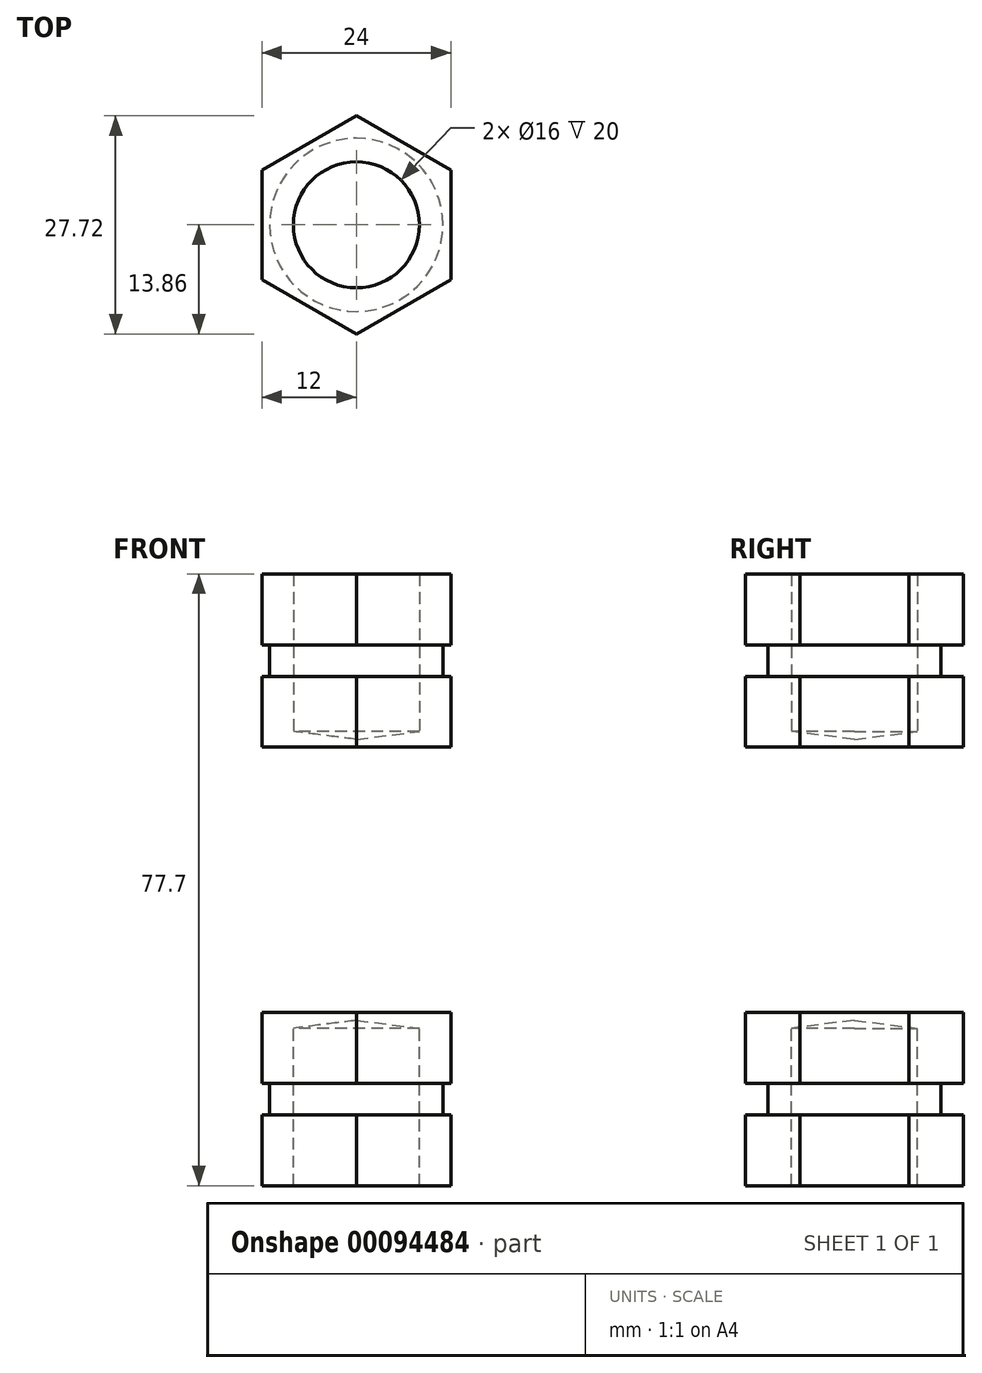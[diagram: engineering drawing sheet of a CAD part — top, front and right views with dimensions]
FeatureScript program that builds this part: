
annotation { "Feature Type Name" : "Feature", "Feature Type Description" : "" }
export const myFeature = defineFeature(function(context is Context, id is Id, definition is map)
    precondition{}
    {
        {
            var Q0;
            Q0=qCreatedBy(makeId("Top.planeOp"),FACE);
            var sketch = newSketch(context, id + "F0", { "sketchPlane" : qUnion([Q0])});
            skCircle(sketch, "E0", {"center": v(0, 0) * mm, "radius": 40.85 * mm});
            skSolve(sketch);
        }
        {
            var Q0;
            Q0=makeQuery(id+"F0.imprint","IMPRINT",FACE,{"disambiguationData":[TD([[makeQuery(id+"F0.imprint","IMPRINT",EDGE,{"derivedFrom":sQuery(id+"F0.wireOp",EDGE,"E0")}),1.0]])]});
            extrude(context, id + "F1", {"entities" : qUnion([Q0]), "depth" : 77.7 * mm});
        }
        {
            var Q0;
            Q0=makeQuery(id+"F1.opExtrude","CAP_FACE",FACE,{"disambiguationData":[OSD([sQuery(id+"F0.wireOp",EDGE,"E0")])],"isStart":true});
            var sketch = newSketch(context, id + "F2", { "sketchPlane" : qUnion([Q0])});
            skCircle(sketch, "E1.cCircle", {"center": v(0, 0) * mm, "radius": 12 * mm, "construction": true});
            skLineSegment(sketch, "E1.0", {"start": v(12, 6.93) * mm, "end": v(12, -6.93) * mm});
            skLineSegment(sketch, "E1.1", {"start": v(12, -6.93) * mm, "end": v(0, -13.86) * mm});
            skLineSegment(sketch, "E1.2", {"start": v(0, -13.86) * mm, "end": v(-12, -6.93) * mm});
            skLineSegment(sketch, "E1.3", {"start": v(-12, -6.93) * mm, "end": v(-12, 6.93) * mm});
            skLineSegment(sketch, "E1.4", {"start": v(-12, 6.93) * mm, "end": v(0, 13.86) * mm});
            skLineSegment(sketch, "E1.5", {"start": v(0, 13.86) * mm, "end": v(12, 6.93) * mm});
            skPoint(sketch, "E1.0.midPoint", {"position": v(12, 0) * mm});
            skCircle(sketch, "E2", {"center": v(0, 0) * mm, "radius": 8 * mm});
            skSolve(sketch);
        }
        {
            var Q0;
            Q0=makeQuery(id+"F2.imprint","IMPRINT",FACE,{"disambiguationData":[TD([[makeQuery(id+"F2.imprint","IMPRINT",EDGE,{"derivedFrom":sQuery(id+"F2.wireOp",EDGE,"E1.0")}),-1.0]])]});
            var Q1;
            Q1=makeQuery(id+"F2.imprint","IMPRINT",FACE,{"disambiguationData":[TD([[makeQuery(id+"F2.imprint","IMPRINT",EDGE,{"derivedFrom":sQuery(id+"F2.wireOp",EDGE,"E2")}),1.0]])]});
            extrude(context, id + "F3", {"entities" : qUnion([Q0, Q1]), "oppositeDirection" : true, "depth" : 22 * mm});
        }
        {
            var Q0;
            Q0=makeQuery(id+"F3.opExtrude","CAP_FACE",FACE,{"disambiguationData":[OSD([sQuery(id+"F2.wireOp",EDGE,"E1.0"),sQuery(id+"F2.wireOp",EDGE,"E1.1"),sQuery(id+"F2.wireOp",EDGE,"E1.2"),sQuery(id+"F2.wireOp",EDGE,"E1.3"),sQuery(id+"F2.wireOp",EDGE,"E1.4"),sQuery(id+"F2.wireOp",EDGE,"E1.5")])],"isStart":true});
            var sketch = newSketch(context, id + "F4", { "sketchPlane" : qUnion([Q0])});
            skCircle(sketch, "E3", {"center": v(0, 0) * mm, "radius": 15 * mm});
            skCircle(sketch, "E4", {"center": v(0, 0) * mm, "radius": 11 * mm});
            skSolve(sketch);
        }
        {
            var Q0;
            Q0=makeQuery(id+"F4.imprint","IMPRINT",FACE,{"disambiguationData":[TD([[makeQuery(id+"F4.imprint","IMPRINT",EDGE,{"derivedFrom":sQuery(id+"F4.wireOp",EDGE,"E3")}),1.0]])]});
            var Q1;
            Q1=makeQuery(id+"F4.imprint","IMPRINT",FACE,{"disambiguationData":[TD([[makeQuery(id+"F4.imprint","IMPRINT",EDGE,{"derivedFrom":sQuery(id+"F4.wireOp",EDGE,"E4")}),-1.0]])]});
            extrude(context, id + "F5", {"entities" : qUnion([Q0, Q1]), "operationType" : NewBodyOperationType.REMOVE, "oppositeDirection" : true, "depth" : 13 * mm, "hasSecondDirection" : true, "secondDirectionOppositeDirection" : true, "secondDirectionDepth" : 9 * mm});
        }
        {
            var Q0;
            Q0=makeQuery(id+"F3.opExtrude","SWEPT_BODY",BODY,{"disambiguationData":[OSD([sQuery(id+"F2.wireOp",EDGE,"E1.0"),sQuery(id+"F2.wireOp",EDGE,"E1.1"),sQuery(id+"F2.wireOp",EDGE,"E1.2"),sQuery(id+"F2.wireOp",EDGE,"E1.3"),sQuery(id+"F2.wireOp",EDGE,"E1.4"),sQuery(id+"F2.wireOp",EDGE,"E1.5")])]});
            var Q1;
            Q1=makeQuery(id+"F1.opExtrude","SWEPT_BODY",BODY,{"disambiguationData":[OSD([sQuery(id+"F0.wireOp",EDGE,"E0")])]});
            booleanBodies(context, id + "F6", {"operationType" : BooleanOperationType.SUBTRACTION, "tools" : qUnion([Q0]), "targets" : qUnion([Q1]), "keepTools" : true});
        }
        {
            var Q0;
            Q0=qCreatedBy(makeId("Front.planeOp"),FACE);
            var sketch = newSketch(context, id + "F7", { "sketchPlane" : qUnion([Q0])});
            skLineSegment(sketch, "E5", {"start": v(0, 0) * mm, "end": v(0, 21) * mm});
            skLineSegment(sketch, "E6", {"start": v(0, 21) * mm, "end": v(8, 20) * mm});
            skLineSegment(sketch, "E7", {"start": v(8, 20) * mm, "end": v(8, 0) * mm});
            skLineSegment(sketch, "E8", {"start": v(8, 0) * mm, "end": v(0, 0) * mm});
            skSolve(sketch);
        }
        {
            var Q0;
            Q0=makeQuery(id+"F7.imprint","IMPRINT",FACE,{"disambiguationData":[TD([[makeQuery(id+"F7.imprint","IMPRINT",EDGE,{"derivedFrom":sQuery(id+"F7.wireOp",EDGE,"E5")}),-1.0]])]});
            var Q1;
            Q1=sQuery(id+"F7.wireOp",EDGE,"E5");
            revolve(context, id + "F8", {"operationType" : NewBodyOperationType.REMOVE, "entities" : qUnion([Q0]), "axis" : qUnion([Q1]), "revolveType" : RevolveType.FULL, "oppositeDirection" : true});
        }
        {
            var Q0;
            Q0=makeQuery(id+"F3.opExtrude","SWEPT_BODY",BODY,{"disambiguationData":[OSD([sQuery(id+"F2.wireOp",EDGE,"E1.0"),sQuery(id+"F2.wireOp",EDGE,"E1.1"),sQuery(id+"F2.wireOp",EDGE,"E1.2"),sQuery(id+"F2.wireOp",EDGE,"E1.3"),sQuery(id+"F2.wireOp",EDGE,"E1.4"),sQuery(id+"F2.wireOp",EDGE,"E1.5")])]});
            var Q1;
            Q1=qCreatedBy(makeId("Top.planeOp"),FACE);
            mirror(context, id + "F9", {"entities" : qUnion([Q0]), "mirrorPlane" : qUnion([Q1])});
        }
        {
            var Q0;
            Q0=makeQuery(id+"F9.opPattern","COPY",BODY,{"derivedFrom":makeQuery(id+"F3.opExtrude","SWEPT_BODY",BODY,{"disambiguationData":[OSD([sQuery(id+"F2.wireOp",EDGE,"E1.0"),sQuery(id+"F2.wireOp",EDGE,"E1.1"),sQuery(id+"F2.wireOp",EDGE,"E1.2"),sQuery(id+"F2.wireOp",EDGE,"E1.3"),sQuery(id+"F2.wireOp",EDGE,"E1.4"),sQuery(id+"F2.wireOp",EDGE,"E1.5")])]}),"instanceName":"1"});
            transform(context, id + "F10", {"entities" : qUnion([Q0]), "transformType" : TransformType.TRANSLATION_3D, "dx" : 0 * mm, "dy" : 0 * mm, "dz" : 77.7 * mm, "makeCopy" : false});
        }
        {
            var Q0;
            Q0=makeQuery(id+"F9.opPattern","COPY",BODY,{"derivedFrom":makeQuery(id+"F3.opExtrude","SWEPT_BODY",BODY,{"disambiguationData":[OSD([sQuery(id+"F2.wireOp",EDGE,"E1.0"),sQuery(id+"F2.wireOp",EDGE,"E1.1"),sQuery(id+"F2.wireOp",EDGE,"E1.2"),sQuery(id+"F2.wireOp",EDGE,"E1.3"),sQuery(id+"F2.wireOp",EDGE,"E1.4"),sQuery(id+"F2.wireOp",EDGE,"E1.5")])]}),"instanceName":"1"});
            var Q1;
            Q1=makeQuery(id+"F1.opExtrude","SWEPT_BODY",BODY,{"disambiguationData":[OSD([sQuery(id+"F0.wireOp",EDGE,"E0")])]});
            booleanBodies(context, id + "F11", {"operationType" : BooleanOperationType.SUBTRACTION, "tools" : qUnion([Q0]), "targets" : qUnion([Q1]), "keepTools" : true});
        }
        {
            var Q0;
            Q0=makeQuery(id+"F11.opBoolean","SPLIT",BODY,{"disambiguationData":[OD(1.0)],"derivedFrom":makeQuery(id+"F1.opExtrude","SWEPT_BODY",BODY,{"disambiguationData":[OSD([sQuery(id+"F0.wireOp",EDGE,"E0")])]})});
            deleteBodies(context, id + "F12", {"entities" : qUnion([Q0])});
        }
    });
